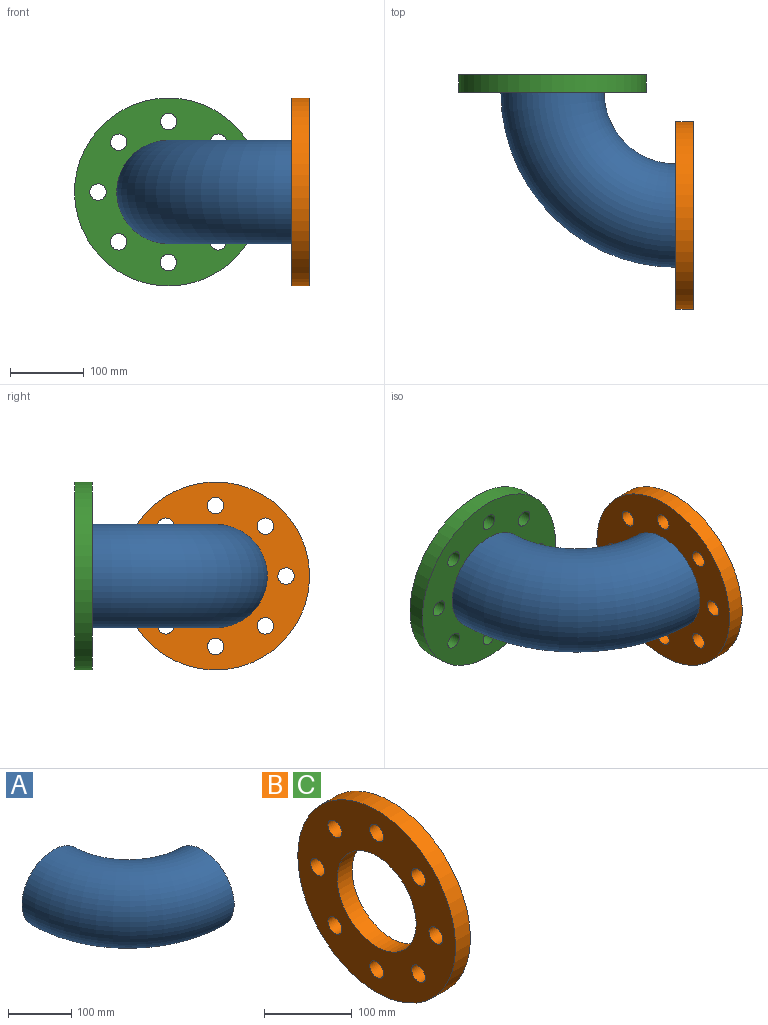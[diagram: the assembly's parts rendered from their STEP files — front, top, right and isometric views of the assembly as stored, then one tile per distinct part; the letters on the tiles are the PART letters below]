
ASSEMBLY  parts=3 mates=1
PART A: 4 faces, bbox 256x256x139.7 mm
  f0: torus R=166.69mm, axis (0,0,1), area 104466.4mm2, adj f2,f3
  f1: torus R=166.69mm, axis (0,0,1), area 114913mm2, adj f2,f3
  f2: plane 139.7x139.7mm, normal (0,1,0), area 2660.2mm2, adj f0,f1
  f3: plane 139.7x139.7mm, normal (1,0,0), area 2660.2mm2, adj f0,f1
PART B: 12 faces, bbox 23.8x254x254 mm
  f0: cylinder r=63.5mm len=127mm, axis (-1,0,0), area 9500.8mm2, adj f10,f11
  f1: cylinder r=11.11mm len=23.81mm, axis (-1,0,0), area 1662.6mm2, adj f10,f11
  f2: cylinder r=11.11mm len=23.81mm, axis (-1,0,0), area 1662.6mm2, adj f10,f11
  f3: cylinder r=11.11mm len=23.81mm, axis (-1,0,0), area 1662.6mm2, adj f10,f11
  f4: cylinder r=11.11mm len=23.81mm, axis (-1,0,0), area 1662.6mm2, adj f10,f11
  f5: cylinder r=11.11mm len=23.81mm, axis (-1,0,0), area 1662.6mm2, adj f10,f11
  f6: cylinder r=11.11mm len=23.81mm, axis (-1,0,0), area 1662.6mm2, adj f10,f11
  f7: cylinder r=11.11mm len=23.81mm, axis (-1,0,0), area 1662.6mm2, adj f10,f11
  f8: cylinder r=11.11mm len=23.81mm, axis (-1,0,0), area 1662.6mm2, adj f10,f11
  f9: cylinder r=127mm len=254mm, axis (-1,0,0), area 19001.5mm2, adj f10,f11
  f10: plane 254x254mm, normal (1,0,0), area 34899.5mm2, adj f0,f1,f2,f3,f4,f5,f6,f7
  f11: plane 254x254mm, normal (-1,0,0), area 34899.5mm2, adj f0,f1,f2,f3,f4,f5,f6,f7
PART C: same geometry as B
PLACE A t=(-34.81,-10.68,3.81)mm
PLACE B t=(-34.81,-10.68,3.81)mm
PLACE C rot(axis=(0.58,-0.58,-0.58),120deg) t=(-201.5,179.82,3.81)mm
MATE fastened C.f0 <-> A.f2  axis (0,-1,0) through (-201.5,156,3.81)mm
